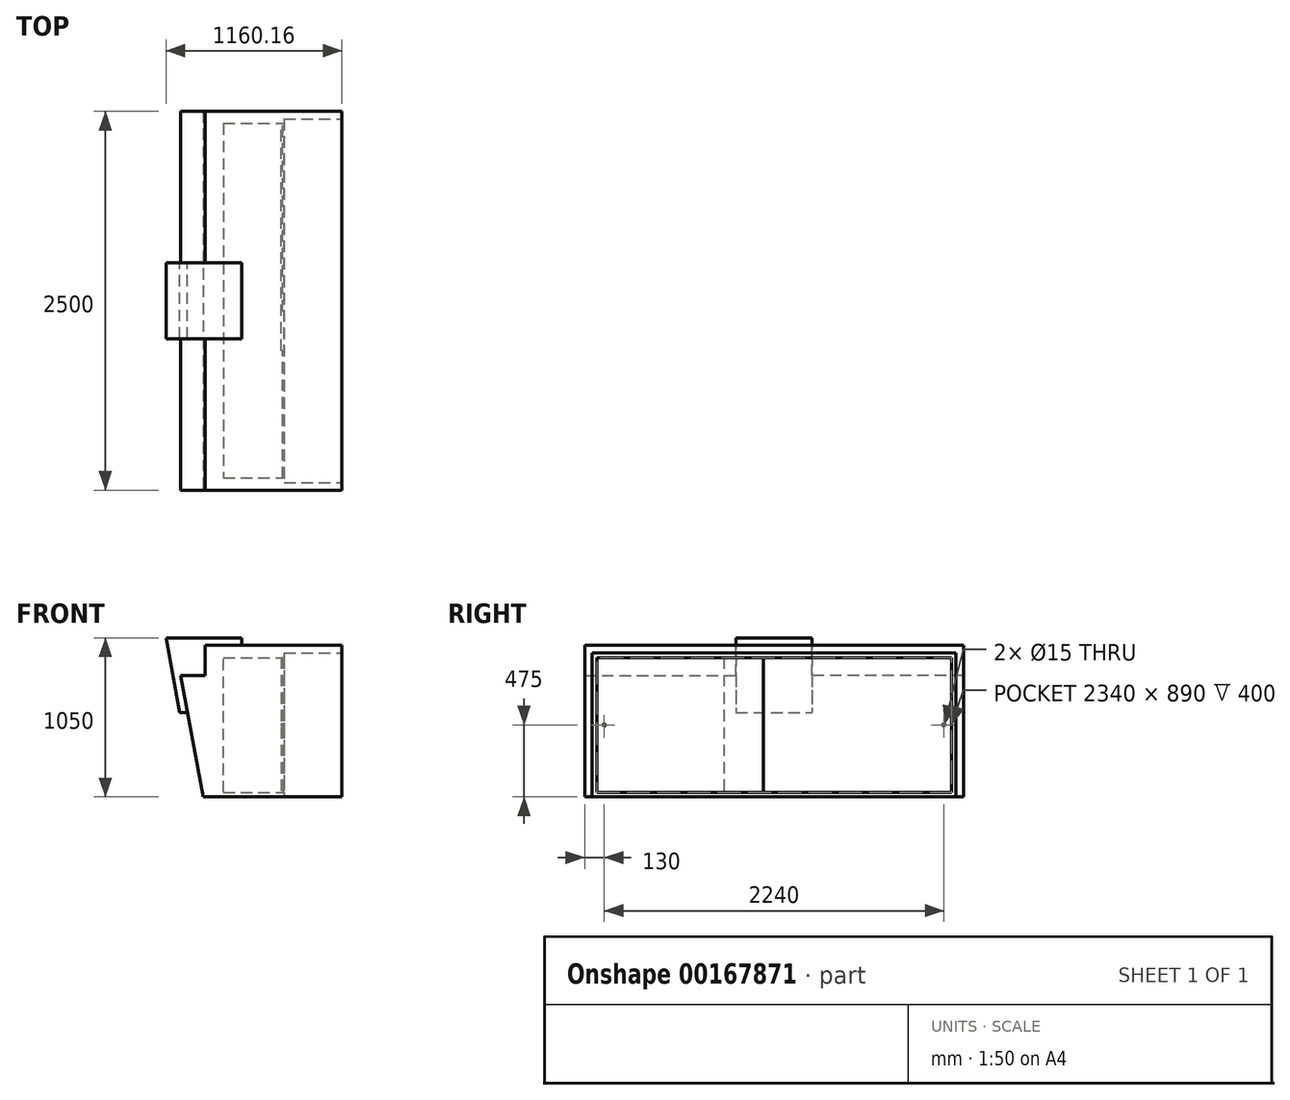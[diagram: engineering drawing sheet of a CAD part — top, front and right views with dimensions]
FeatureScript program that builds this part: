
annotation { "Feature Type Name" : "Feature", "Feature Type Description" : "" }
export const myFeature = defineFeature(function(context is Context, id is Id, definition is map)
    precondition{}
    {
        {
            var Q0;
            Q0=qCreatedBy(makeId("Top.planeOp"),FACE);
            var sketch = newSketch(context, id + "F0", { "sketchPlane" : qUnion([Q0])});
            skLineSegment(sketch, "E0.bottom", {"start": v(457, 1250) * mm, "end": v(-457, 1250) * mm});
            skLineSegment(sketch, "E0.top", {"start": v(457, -1250) * mm, "end": v(-457, -1250) * mm});
            skLineSegment(sketch, "E0.left", {"start": v(457, 1250) * mm, "end": v(457, -1250) * mm});
            skLineSegment(sketch, "E0.right", {"start": v(-457, 1250) * mm, "end": v(-457, -1250) * mm});
            skPoint(sketch, "E0.middle", {"position": v(0, 0) * mm});
            skSolve(sketch);
        }
        {
            var Q0;
            Q0=qCreatedBy(makeId("Top.planeOp"),FACE);
            cPlane(context, id + "F1", {"entities" : qUnion([Q0]), "cplaneType" : CPlaneType.OFFSET, "offset" : 1000 * mm, "width" : 150 * mm, "height" : 150 * mm});
        }
        {
            var Q0;
            Q0=qCreatedBy(id+"F1.planeOp",FACE);
            var sketch = newSketch(context, id + "F2", { "sketchPlane" : qUnion([Q0])});
            skLineSegment(sketch, "E1.bottom", {"start": v(457, 1250) * mm, "end": v(-643, 1250) * mm});
            skLineSegment(sketch, "E1.top", {"start": v(457, -1250) * mm, "end": v(-643, -1250) * mm});
            skLineSegment(sketch, "E1.left", {"start": v(457, 1250) * mm, "end": v(457, -1250) * mm});
            skLineSegment(sketch, "E1.right", {"start": v(-643, 1250) * mm, "end": v(-643, -1250) * mm});
            skSolve(sketch);
        }
        {
            var Q0;
            Q0=makeQuery(id+"F2.imprint","IMPRINT",FACE,{"disambiguationData":[TD([[makeQuery(id+"F2.imprint","IMPRINT",EDGE,{"derivedFrom":sQuery(id+"F2.wireOp",EDGE,"E1.bottom")}),1.0]])]});
            var Q1;
            Q1=makeQuery(id+"F0.imprint","IMPRINT",FACE,{"disambiguationData":[TD([[makeQuery(id+"F0.imprint","IMPRINT",EDGE,{"derivedFrom":sQuery(id+"F0.wireOp",EDGE,"E0.bottom")}),1.0]])]});
            loft(context, id + "F3", {"sheetProfilesArray" : [{ "sheetProfileEntities" : qUnion([Q0]) }, { "sheetProfileEntities" : qUnion([Q1]) }]});
        }
        {
            var Q0;
            Q0=makeQuery(id+"F3.opLoft","SWEPT_FACE",FACE,{"disambiguationData":[OSD([sQuery(id+"F0.wireOp",EDGE,"E0.bottom"),sQuery(id+"F0.wireOp",EDGE,"E0.top"),sQuery(id+"F0.wireOp",EDGE,"E0.left"),sQuery(id+"F2.wireOp",EDGE,"E1.bottom"),sQuery(id+"F2.wireOp",EDGE,"E1.top"),sQuery(id+"F2.wireOp",EDGE,"E1.left")])]});
            var sketch = newSketch(context, id + "F4", { "sketchPlane" : qUnion([Q0])});
            skLineSegment(sketch, "E2.0", {"start": v(-1200, 950) * mm, "end": v(-1200, 0) * mm});
            skLineSegment(sketch, "E2.1", {"start": v(1200, 950) * mm, "end": v(-1200, 950) * mm});
            skLineSegment(sketch, "E2.2", {"start": v(1200, 0) * mm, "end": v(1200, 950) * mm});
            skLineSegment(sketch, "E2.3", {"start": v(-1200, 50) * mm, "end": v(1200, 50) * mm, "construction": true});
            skSolve(sketch);
        }
        {
            var Q0;
            {var subQ0=sQuery(id+"F4.wireOp",EDGE,"E2.0");Q0=makeQuery(id+"F4.imprint","IMPRINT",FACE,{"disambiguationData":[TD([[makeQuery(id+"F4.imprint","IMPRINT",EDGE,{"derivedFrom":subQ0}),1.0]])]});}
            extrude(context, id + "F5", {"entities" : qUnion([Q0]), "operationType" : NewBodyOperationType.REMOVE, "oppositeDirection" : true, "depth" : 381 * mm});
        }
        {
            var Q0;
            Q0=makeQuery(id+"F5.boolean.opBoolean","COPY",FACE,{"derivedFrom":makeQuery(id+"F5.opExtrude","CAP_FACE",FACE,{"disambiguationData":[OSD([sQuery(id+"F0.wireOp",EDGE,"E0.bottom"),sQuery(id+"F0.wireOp",EDGE,"E0.top"),sQuery(id+"F0.wireOp",EDGE,"E0.left"),sQuery(id+"F4.wireOp",EDGE,"E2.0"),sQuery(id+"F4.wireOp",EDGE,"E2.1"),sQuery(id+"F4.wireOp",EDGE,"E2.2")])],"isStart":false})});
            var sketch = newSketch(context, id + "F6", { "sketchPlane" : qUnion([Q0])});
            skLineSegment(sketch, "E3.0", {"start": v(1170, 920) * mm, "end": v(-1170, 920) * mm});
            skLineSegment(sketch, "E3.1", {"start": v(1170, 30) * mm, "end": v(1170, 920) * mm});
            skLineSegment(sketch, "E3.2", {"start": v(-1170, 30) * mm, "end": v(1170, 30) * mm});
            skLineSegment(sketch, "E3.3", {"start": v(-1170, 920) * mm, "end": v(-1170, 30) * mm});
            skSolve(sketch);
        }
        {
            var Q0;
            Q0=makeQuery(id+"F6.imprint","IMPRINT",FACE,{"disambiguationData":[TD([[makeQuery(id+"F6.imprint","IMPRINT",EDGE,{"derivedFrom":sQuery(id+"F6.wireOp",EDGE,"E3.0")}),1.0]])]});
            extrude(context, id + "F7", {"entities" : qUnion([Q0]), "operationType" : NewBodyOperationType.REMOVE, "oppositeDirection" : true, "depth" : 400 * mm});
        }
        {
            var Q0;
            Q0=makeQuery(id+"F7.boolean.opBoolean","COPY",FACE,{"derivedFrom":makeQuery(id+"F7.opExtrude","SWEPT_FACE",FACE,{"disambiguationData":[OSD([sQuery(id+"F6.wireOp",EDGE,"E3.2")])]})});
            var sketch = newSketch(context, id + "F8", { "sketchPlane" : qUnion([Q0])});
            skLineSegment(sketch, "E4.bottom", {"start": v(76, -1170) * mm, "end": v(66, -1170) * mm});
            skLineSegment(sketch, "E4.top", {"start": v(76, -70) * mm, "end": v(66, -70) * mm});
            skLineSegment(sketch, "E4.left", {"start": v(76, -1170) * mm, "end": v(76, -70) * mm});
            skLineSegment(sketch, "E4.right", {"start": v(66, -1170) * mm, "end": v(66, -70) * mm});
            skPoint(sketch, "E5.orphan", {"position": v(0, -70) * mm});
            skLineSegment(sketch, "E6.bottom", {"start": v(66, -330) * mm, "end": v(56, -330) * mm});
            skLineSegment(sketch, "E6.top", {"start": v(66, 1170) * mm, "end": v(56, 1170) * mm});
            skLineSegment(sketch, "E6.left", {"start": v(66, -330) * mm, "end": v(66, 1170) * mm});
            skLineSegment(sketch, "E6.right", {"start": v(56, -330) * mm, "end": v(56, 1170) * mm});
            skPoint(sketch, "E7.orphan", {"position": v(0, 1170) * mm});
            skSolve(sketch);
        }
        {
            var Q0;
            Q0 = qSketchRegion(id + "F8", true);
            var Q1;
            Q1=makeQuery(id+"F7.boolean.opBoolean","COPY",FACE,{"derivedFrom":makeQuery(id+"F7.opExtrude","SWEPT_FACE",FACE,{"disambiguationData":[OSD([sQuery(id+"F6.wireOp",EDGE,"E3.0")])]})});
            extrude(context, id + "F9", {"entities" : qUnion([Q0]), "endBound" : BoundingType.UP_TO_SURFACE, "endBoundEntityFace" : qUnion([Q1]), "depth" : 25 * mm});
        }
        {
            var Q0;
            Q0=makeQuery(id+"F9.opExtrude","SWEPT_FACE",FACE,{"disambiguationData":[OSD([sQuery(id+"F8.wireOp",EDGE,"E4.left")])]});
            var sketch = newSketch(context, id + "F10", { "sketchPlane" : qUnion([Q0])});
            skCircle(sketch, "E8", {"center": v(-1120, 475) * mm, "radius": 7.5 * mm});
            skPoint(sketch, "E8.centerSnap0", {"position": v(-1170, 475) * mm});
            skCircle(sketch, "E9", {"center": v(1120, 475) * mm, "radius": 7.5 * mm});
            skSolve(sketch);
        }
        {
            var Q0;
            Q0 = qSketchRegion(id + "F10", true);
            extrude(context, id + "F11", {"entities" : qUnion([Q0]), "operationType" : NewBodyOperationType.REMOVE, "oppositeDirection" : true, "depth" : 50 * mm, "hasSecondDirection" : true, "secondDirectionOppositeDirection" : false, "secondDirectionDepth" : 60 * mm});
        }
        {
            var Q0;
            Q0=qCreatedBy(makeId("Front.planeOp"),FACE);
            var sketch = newSketch(context, id + "F12", { "sketchPlane" : qUnion([Q0])});
            skLineSegment(sketch, "E10.bottom", {"start": v(-643, 1000) * mm, "end": v(-443, 1000) * mm});
            skLineSegment(sketch, "E10.top", {"start": v(-643, 800) * mm, "end": v(-443, 800) * mm});
            skLineSegment(sketch, "E10.left", {"start": v(-643, 1000) * mm, "end": v(-643, 800) * mm});
            skLineSegment(sketch, "E10.right", {"start": v(-443, 1000) * mm, "end": v(-443, 800) * mm});
            skSolve(sketch);
        }
        {
            var Q0;
            Q0 = qSketchRegion(id + "F12", true);
            extrude(context, id + "F13", {"entities" : qUnion([Q0]), "operationType" : NewBodyOperationType.REMOVE, "endBound" : BoundingType.THROUGH_ALL, "oppositeDirection" : true, "depth" : 2400 * mm, "hasSecondDirection" : true, "secondDirectionBound" : SecondDirectionBoundingType.THROUGH_ALL, "secondDirectionOppositeDirection" : false, "secondDirectionDepth" : 25 * mm});
        }
        {
            var Q0;
            Q0=qCreatedBy(makeId("Front.planeOp"),FACE);
            var sketch = newSketch(context, id + "F14", { "sketchPlane" : qUnion([Q0])});
            skLineSegment(sketch, "E11", {"start": v(-203.16, 1050) * mm, "end": v(-703.16, 1050) * mm});
            skLineSegment(sketch, "E12", {"start": v(-703.16, 1050) * mm, "end": v(-611.73, 558.43) * mm});
            skLineSegment(sketch, "E13", {"start": v(-203.16, 1050) * mm, "end": v(-203.16, 952.67) * mm});
            skLineSegment(sketch, "E14", {"start": v(-203.16, 952.67) * mm, "end": v(-384.94, 952.67) * mm});
            skLineSegment(sketch, "E15", {"start": v(-384.94, 952.67) * mm, "end": v(-384.94, 558.43) * mm});
            skLineSegment(sketch, "E16", {"start": v(-384.94, 558.43) * mm, "end": v(-611.73, 558.43) * mm});
            skSolve(sketch);
        }
        {
            var Q0;
            Q0=makeQuery(id+"F14.imprint","IMPRINT",FACE,{"disambiguationData":[TD([[makeQuery(id+"F14.imprint","IMPRINT",EDGE,{"derivedFrom":sQuery(id+"F14.wireOp",EDGE,"E11")}),1.0]])]});
            extrude(context, id + "F15", {"entities" : qUnion([Q0]), "operationType" : NewBodyOperationType.ADD, "endBound" : BoundingType.SYMMETRIC, "depth" : 500 * mm});
        }
    });
